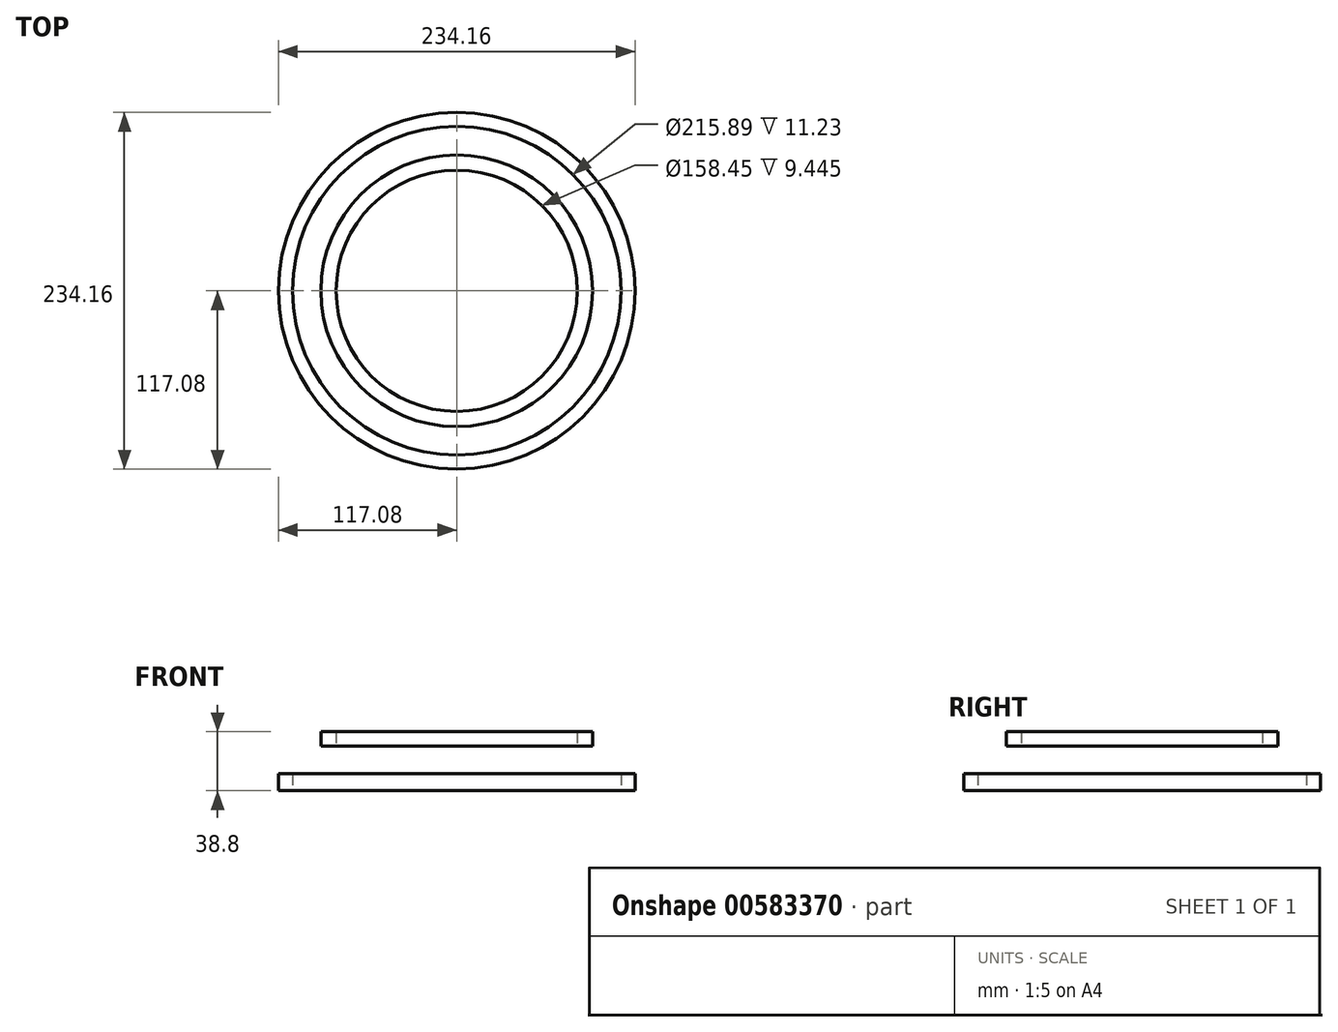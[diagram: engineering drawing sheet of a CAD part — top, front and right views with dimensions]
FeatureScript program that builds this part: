
annotation { "Feature Type Name" : "Feature", "Feature Type Description" : "" }
export const myFeature = defineFeature(function(context is Context, id is Id, definition is map)
    precondition{}
    {
        {
            var Q0;
            Q0=qCreatedBy(makeId("Top.planeOp"),FACE);
            var sketch = newSketch(context, id + "F0", { "sketchPlane" : qUnion([Q0])});
            skCircle(sketch, "E0", {"center": v(0, 0) * mm, "radius": 79.23 * mm});
            skCircle(sketch, "E1.0", {"center": v(0, 0) * mm, "radius": 89.23 * mm});
            skSolve(sketch);
        }
        {
            var Q0;
            Q0=makeQuery(id+"F0.imprint","IMPRINT",FACE,{"disambiguationData":[TD([[makeQuery(id+"F0.imprint","IMPRINT",EDGE,{"derivedFrom":sQuery(id+"F0.wireOp",EDGE,"E0")}),-1.0]])]});
            extrude(context, id + "F1", {"entities" : qUnion([Q0]), "depth" : 9.44 * mm, "offsetDistance" : 25 * mm});
        }
        {
            var Q0;
            Q0=makeQuery(id+"F1.opExtrude","CAP_FACE",FACE,{"disambiguationData":[OSD([sQuery(id+"F0.wireOp",EDGE,"E0"),sQuery(id+"F0.wireOp",EDGE,"E1.0")])],"isStart":false});
            cPlane(context, id + "F2", {"entities" : qUnion([Q0]), "cplaneType" : CPlaneType.OFFSET, "offset" : 38.8 * mm, "oppositeDirection" : true, "width" : 150 * mm, "height" : 150 * mm});
        }
        {
            var Q0;
            Q0=qCreatedBy(id+"F2.planeOp",FACE);
            var sketch = newSketch(context, id + "F3", { "sketchPlane" : qUnion([Q0])});
            skCircle(sketch, "E2", {"center": v(0, 0) * mm, "radius": 107.94 * mm});
            skCircle(sketch, "E3.0", {"center": v(0, 0) * mm, "radius": 117.08 * mm});
            skSolve(sketch);
        }
        {
            var Q0;
            Q0=makeQuery(id+"F3.imprint","IMPRINT",FACE,{"disambiguationData":[TD([[makeQuery(id+"F3.imprint","IMPRINT",EDGE,{"derivedFrom":sQuery(id+"F3.wireOp",EDGE,"E2")}),-1.0]])]});
            extrude(context, id + "F4", {"entities" : qUnion([Q0]), "depth" : 11.23 * mm, "offsetDistance" : 25 * mm});
        }
        {
            var Q0;
            Q0=qCreatedBy(id+"F2.planeOp",FACE);
            cPlane(context, id + "F5", {"entities" : qUnion([Q0]), "cplaneType" : CPlaneType.OFFSET, "offset" : 64.14 * mm, "oppositeDirection" : true, "width" : 150 * mm, "height" : 150 * mm});
        }
        {
            var Q0;
            Q0=qCreatedBy(id+"F5.planeOp",FACE);
            var sketch = newSketch(context, id + "F6", { "sketchPlane" : qUnion([Q0])});
            skCircle(sketch, "E4.cCircle", {"center": v(0, 0) * mm, "radius": 118.14 * mm});
            skLineSegment(sketch, "E4.0", {"start": v(-13.27, -135.77) * mm, "end": v(-124.21, -56.4) * mm});
            skLineSegment(sketch, "E4.1", {"start": v(-124.21, -56.4) * mm, "end": v(-110.94, 79.38) * mm});
            skLineSegment(sketch, "E4.2", {"start": v(-110.94, 79.38) * mm, "end": v(13.27, 135.77) * mm});
            skLineSegment(sketch, "E4.3", {"start": v(13.27, 135.77) * mm, "end": v(124.21, 56.4) * mm});
            skLineSegment(sketch, "E4.4", {"start": v(124.21, 56.4) * mm, "end": v(110.94, -79.38) * mm});
            skLineSegment(sketch, "E4.5", {"start": v(110.94, -79.38) * mm, "end": v(-13.27, -135.77) * mm});
            skPoint(sketch, "E4.0.midPoint", {"position": v(-68.74, -96.08) * mm});
            skLineSegment(sketch, "E5.0", {"start": v(-12.69, -129.79) * mm, "end": v(-118.74, -53.9) * mm});
            skLineSegment(sketch, "E5.1", {"start": v(-106.05, 75.88) * mm, "end": v(12.69, 129.79) * mm});
            skLineSegment(sketch, "E5.2", {"start": v(12.69, 129.79) * mm, "end": v(118.74, 53.9) * mm});
            skLineSegment(sketch, "E5.3", {"start": v(-118.74, -53.9) * mm, "end": v(-106.05, 75.88) * mm});
            skLineSegment(sketch, "E5.4", {"start": v(118.74, 53.9) * mm, "end": v(106.05, -75.88) * mm});
            skLineSegment(sketch, "E5.5", {"start": v(106.05, -75.88) * mm, "end": v(-12.69, -129.79) * mm});
            skSolve(sketch);
        }
        {
            var Q0;
            Q0=makeQuery(id+"F4.opExtrude","CAP_EDGE",EDGE,{"disambiguationData":[OSD([sQuery(id+"F3.wireOp",EDGE,"E2")])],"isStart":false});
            var Q1;
            Q1=makeQuery(id+"F1.opExtrude","CAP_EDGE",EDGE,{"disambiguationData":[OSD([sQuery(id+"F0.wireOp",EDGE,"E0")])],"isStart":false});
            loft(context, id + "F7", {"bodyType" : ToolBodyType.SURFACE, "wireProfilesArray" : [{ "wireProfileEntities" : qUnion([Q0]) }, { "wireProfileEntities" : qUnion([Q1]) }]});
        }
    });
